# Revit family: Forte 8ft Tower Door Left & Right
name_source: partatom
category: Furniture
revit_build: Autodesk Revit Architecture 2012 (Build: 20110916_2132(x64)
units: mm (PartAtom-declared; Revit-internal decimal feet)

## types (5) — shared parameters
Manufacturer = Wenger Corporation
Model = 60
URL = http://www.wengercorp.com

## per-type parameters (varying)
| type | Description | Tower Height (16', 17', 18', 19', 20') | Tower Label |
| Forte 16' Tower Door Left & Right | Standard 16' Forte Tower | 16' - 0" | Labels : 16ft |
| Forte 17' Tower Door Left & Right | Standard 17ft Forte Tower | 17' - 0" | Labels : 17ft |
| Forte 18' Tower Door Left & Right | Standard 18ft Forte Tower | 18' - 0" | Labels : 18ft |
| Forte 19' Tower Door Left & Right | Standard 19ft Forte Tower | 19' - 0" | Labels : 19ft |
| Forte 20' Tower Door Left & Right | Standard 20ft Forte Tower | 20' - 0" | Labels : 20ft |

## geometry (parser evidence)
native form markers: Blend x10, Sweep x3
no freeform markers — native parametric forms only
